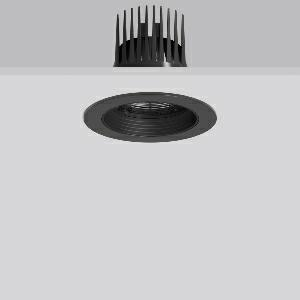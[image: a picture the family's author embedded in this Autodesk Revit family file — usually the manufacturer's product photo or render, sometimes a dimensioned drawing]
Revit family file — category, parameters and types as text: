
# Revit family: heledon_maxi_e_901769_003_2_76_d3b0
name_source: partatom
category: Lighting Fixtures
units: mm (PartAtom-declared; Revit-internal decimal feet)

## family parameters
Cut with Voids When Loaded = No
Host = Face
Light Source = No
Part Type = Normal
Room Calculation Point = No
Round Connector Dimension = Use Diameter
Shared = No

## types (1)
- HELEDON maxi E (1 x LED Modul 927, 3450 lm, 2700)
    Apparent Load = 35 VA
    Approval mark = CE
    CIE Flux Codes = 96 100 100 100 100
    Color Rendering = 92
    Color Temperature = 2700
    Default Elevation = 1800 mm
    Description = Series: HELEDON maxi
Round recessed downlight. Housing: die-cast aluminium, powder-coated. Black plastic ring and recessed LED to prevent glare from the side. Optical assembly with lens made of plastic (polycarbonate) for the best homogeneous light distribution - can be changed without tools. Best colour rendering index Ra>90. Suitable for Recessed ceiling mounting. Installation without tools thanks to spring fastening system. Including separate LED converter with connecting cable 600 mm.High quality converter without flickering and stroboscopic effect. Through-wiring box (5 pole) available as accessory. The following accessories can be mounted without use of tools: interchangeable lenses, decorative glasses, honeycomb louvre, clear and frosted diffusers, white interchangeable plastic ring. 
Colour: deep black, matt (RAL 9005)
Diameter: 162 mm
Height: 3 mm
Cut-out diameter: 152 mm
Recess height: 200 mm
Luminaire: recess height: 135 mm
Lamp: LED
Socket: without socket
Colour temperature: 2700K
Colour rendering index (CRI): 92
System power: 35 W
Rated luminous flux: 3450 lm
Luminous efficiency: 99 lm/W
Control gear: Converter, dimmable, DALI
Protection class: II
Type of protection: IP 20
    Height = 0 mm  [stored 0 ft]
    Lamp = 1 x LED Modul 927
    Lamp Light Flux = 3450 lm
    Lamp count = 1
    Length = 162 mm
    Lifetime = 50000 h
    Luminous efficacy = 99 lm/W
    Manufacturer = RZB
    ModVariant = No
    Model = 901769.003.2.76
    Mounting Place = Ceiling
    Mounting Type = Recessed
    Number of Poles = 1
    OnlyDefault = Yes
    Power Factor = 1
    Product Name = HELEDON maxi E
    Product group = Recessed downlights
    ProductGroupID = 402
    Protection Class = Protection class II
    Protection Degree = IP 20
    RLX_Detail_Level = 1
    RLX_Emergency_Light_Flux = 0 lm
    RLX_Emergency_Type = 0
    RLX_Emergency_Type_DB = No
    RlxData = <blob elided: 121469 chars, md5=d97a36e6>
    Socket = socket
    Standby Power = 0 W
    System Light Flux = 3450 lm
    System Power = 35 W
    Type Comments = Product without accessories
    Type Image = 901663.003.jpg
    URL = http://relux.com
    VarID = ---
    Voltage = 230 V
    Voltage Range = 220-240 V
    Weight = 0.00 kg
    Width = 0 mm  [stored 0 ft]

note: [stored X ft] marks values corroborated as IEEE doubles in the binary element streams (Revit-internal decimal feet)

## geometry (parser evidence)
native form markers: Blend x4, Sweep x11
no freeform markers — native parametric forms only
